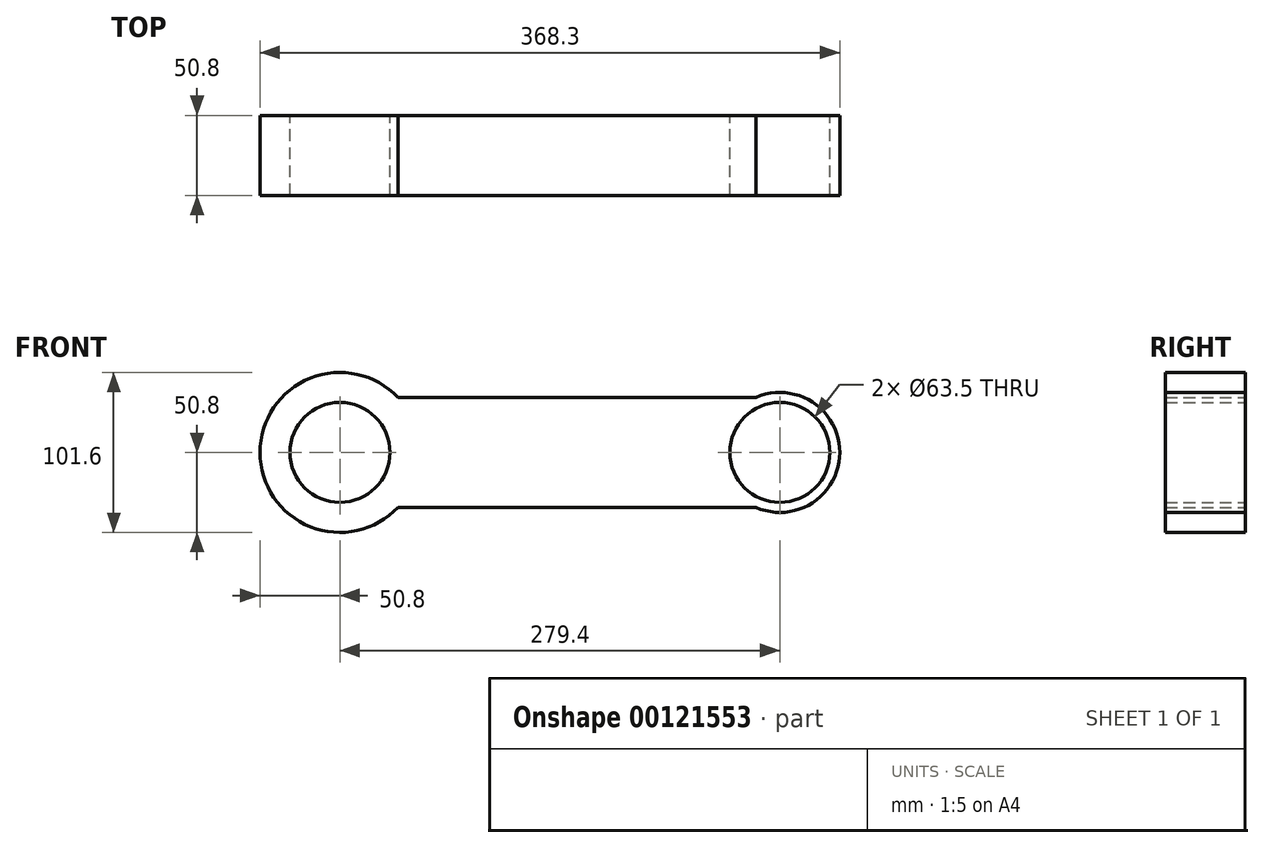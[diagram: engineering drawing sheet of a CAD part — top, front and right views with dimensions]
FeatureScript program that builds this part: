
annotation { "Feature Type Name" : "Feature", "Feature Type Description" : "" }
export const myFeature = defineFeature(function(context is Context, id is Id, definition is map)
    precondition{}
    {
        {
            var Q0;
            Q0=qCreatedBy(makeId("Front.planeOp"),FACE);
            var sketch = newSketch(context, id + "F0", { "sketchPlane" : qUnion([Q0])});
            skCircle(sketch, "E0", {"center": v(0, 0) * mm, "radius": 50.8 * mm});
            skCircle(sketch, "E1", {"center": v(279.4, 0) * mm, "radius": 38.1 * mm});
            skLineSegment(sketch, "E2", {"start": v(0, 0) * mm, "end": v(279.4, 0) * mm, "construction": true});
            skLineSegment(sketch, "E3", {"start": v(36.9, 34.93) * mm, "end": v(294.63, 34.93) * mm});
            skLineSegment(sketch, "E4.MirrorCS", {"start": v(36.9, -34.93) * mm, "end": v(294.63, -34.93) * mm});
            skCircle(sketch, "E5", {"center": v(0, 0) * mm, "radius": 31.75 * mm});
            skCircle(sketch, "E6", {"center": v(279.4, 0) * mm, "radius": 31.75 * mm});
            skSolve(sketch);
        }
        {
            var Q0;
            Q0 = qSketchRegion(id + "F0", true);
            extrude(context, id + "F1", {"entities" : qUnion([Q0]), "depth" : 50.8 * mm});
        }
    });
